# Revit family: Cleanout_Tee-Zurn-Z1445
name_source: partatom
category: Plumbing Fixtures
units: mm (PartAtom-declared; Revit-internal decimal feet)

## family parameters
Always vertical = Yes
Cut with Voids When Loaded = No
Maintain Annotation Orientation = No
OmniClass Number = 23.60.30.11.14
OmniClass Title = Pipework Fittings
Part Type = Normal
Room Calculation Point = No
Round Connector Dimension = Use Radius
Shared = No
Work Plane-Based = No

## types (5) — shared parameters
Assembly Code = D2030100
CW Connection = No
Description = CLEANOUT TEE
HW Connection = No
Main Material = Iron - Zurn - Cast - Painted - Blue
Manufacturer = Zurn Water, LLC
Manufacurer Brand = Zurn
Model = Z1445
Modified Date = 09/19/2025
Product Documentation Link = https://files.zurn.com
Product Page URL = https://www.zurn.com
Product data url = https://www.bimobject.com
URL = www.zurn.com
Vent Connection = No
Waste Connection = Yes
zero-valued in all types: CWFU, Default Elevation, HWFU

## per-type parameters (varying)
| type | A-Pipe Size (Actual Radius) | A-Pipe Size Nominal (Radius) | Approx. Weight (Lbs) | Dimension - B | Dimension C | Dimension D | Inside Void Radius | Tapered Thread Plug Radius | Tapered Thread Plug Radius Outer | Type Comments | WFU |
| 2 NH Pipe Size | 1.25 " | 1 " | 8 " | 6.375 " | 3.875 " | 1.75 " | 0.98 " | 1.125 " | 1.25 " | Z1445 2 Inch No- Hub Outlet | 0 |
| 3 NH Pipe Size | 1.75 " | 1.5 " | 15 " | 7.75 " | 3.875 " | 2.5 " | 1.48 " | 1.625 " | 1.75 " | Z1445 3 Inch No- Hub Outlet | 0 |
| 4 NH Pipe Size | 2.25 " | 2 " | 16 " | 8.875 " | 4.438 " | 3 " | 1.98 " | 2.125 " | 2.25 " | Z1445 4 Inch No- Hub Outlet | 0 |
| 6 NH Pipe Size | 3.313 " | 3 " | 35 " | 12.5 " | 6.25 " | 4.313 " | 2.98 " | 3.125 " | 3.25 " | Z1445 6 Inch No- Hub Outlet | 1 |
| 8 NH Pipe Size | 4.313 " | 4 " | 49 " | 17 " | 8.8 " | 6.375 " | 3.98 " | 4.125 " | 4.25 " | Z1445 8 Inch No- Hub Outlet | 0 |

## geometry (parser evidence)
native form markers: Sweep x3
no freeform markers — native parametric forms only
